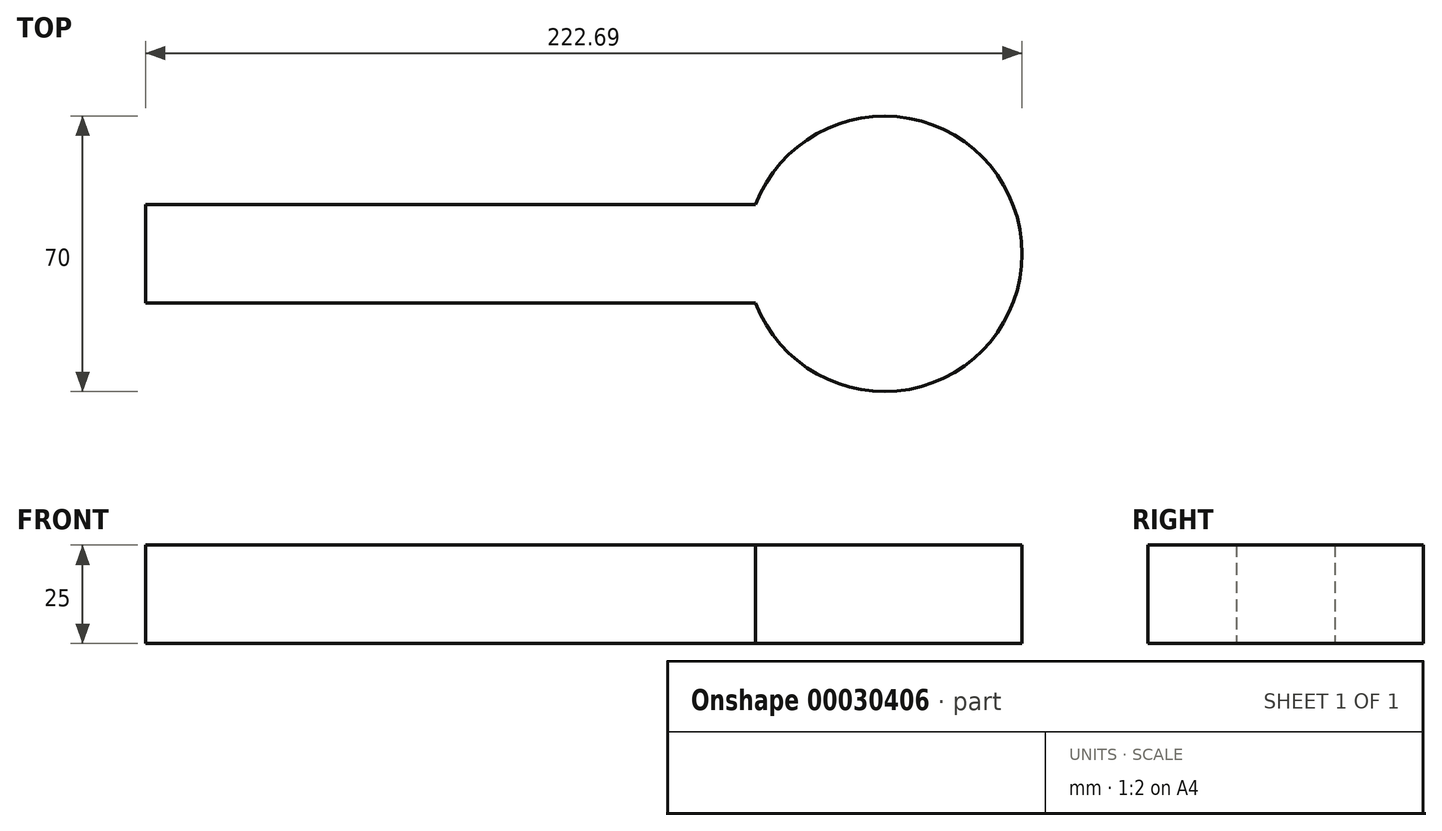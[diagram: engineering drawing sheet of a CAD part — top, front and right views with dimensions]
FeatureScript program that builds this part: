
annotation { "Feature Type Name" : "Feature", "Feature Type Description" : "" }
export const myFeature = defineFeature(function(context is Context, id is Id, definition is map)
    precondition{}
    {
        {
            var Q0;
            Q0=qCreatedBy(makeId("Top.planeOp"),FACE);
            var sketch = newSketch(context, id + "F0", { "sketchPlane" : qUnion([Q0])});
            skLineSegment(sketch, "E0.bottom", {"start": v(-86.93, 32.25) * mm, "end": v(68.07, 32.25) * mm});
            skLineSegment(sketch, "E0.top", {"start": v(-86.93, 7.25) * mm, "end": v(68.07, 7.25) * mm});
            skLineSegment(sketch, "E0.left", {"start": v(-86.93, 32.25) * mm, "end": v(-86.93, 7.25) * mm});
            skLineSegment(sketch, "E0.right", {"start": v(68.07, 32.25) * mm, "end": v(68.07, 7.25) * mm});
            skLineSegment(sketch, "E1.bottom", {"start": v(-86.93, 7.25) * mm, "end": v(-76.93, 7.25) * mm});
            skLineSegment(sketch, "E1.top", {"start": v(-86.93, -22.75) * mm, "end": v(-76.93, -22.75) * mm});
            skLineSegment(sketch, "E1.left", {"start": v(-86.93, 7.25) * mm, "end": v(-86.93, -22.75) * mm});
            skLineSegment(sketch, "E1.right", {"start": v(-76.93, 7.25) * mm, "end": v(-76.93, -22.75) * mm});
            skLineSegment(sketch, "E2.bottom", {"start": v(-69.04, 7.25) * mm, "end": v(-61.04, 7.25) * mm});
            skLineSegment(sketch, "E2.top", {"start": v(-69.04, -7.75) * mm, "end": v(-61.04, -7.75) * mm});
            skLineSegment(sketch, "E2.left", {"start": v(-69.04, 7.25) * mm, "end": v(-69.04, -7.75) * mm});
            skLineSegment(sketch, "E2.right", {"start": v(-61.04, 7.25) * mm, "end": v(-61.04, -7.75) * mm});
            skLineSegment(sketch, "E3", {"start": v(-52.63, 7.25) * mm, "end": v(-38.63, 7.25) * mm});
            skLineSegment(sketch, "E4", {"start": v(-38.63, 7.25) * mm, "end": v(-45.63, -7.75) * mm});
            skLineSegment(sketch, "E5", {"start": v(-45.63, -7.75) * mm, "end": v(-52.63, 7.25) * mm});
            skLineSegment(sketch, "E6", {"start": v(-45.63, 7.25) * mm, "end": v(-38.63, 7.25) * mm});
            skArc(sketch, "E7", {"start": v(68.07, 7.25) * mm, "mid": v(135.76, 19.75) * mm, "end": v(68.07, 32.25) * mm});
            skCircle(sketch, "E8", {"center": v(100.76, 19.75) * mm, "radius": 17.5 * mm});
            skLineSegment(sketch, "E9", {"start": v(-86.93, 19.75) * mm, "end": v(100.76, 19.75) * mm, "construction": true});
            skSolve(sketch);
        }
        {
            var Q0;
            Q0=makeQuery(id+"F0.imprint","IMPRINT",FACE,{"disambiguationData":[TD([[makeQuery(id+"F0.imprint","IMPRINT",EDGE,{"derivedFrom":sQuery(id+"F0.wireOp",EDGE,"E1.bottom")}),-1.0]])]});
            var Q1;
            Q1=makeQuery(id+"F0.imprint","IMPRINT",FACE,{"disambiguationData":[TD([[makeQuery(id+"F0.imprint","IMPRINT",EDGE,{"derivedFrom":sQuery(id+"F0.wireOp",EDGE,"E0.bottom")}),-1.0]])]});
            var Q2;
            Q2=makeQuery(id+"F0.imprint","IMPRINT",FACE,{"disambiguationData":[TD([[makeQuery(id+"F0.imprint","IMPRINT",EDGE,{"derivedFrom":sQuery(id+"F0.wireOp",EDGE,"E3")}),-1.0]])]});
            var Q3;
            Q3=makeQuery(id+"F0.imprint","IMPRINT",FACE,{"disambiguationData":[TD([[makeQuery(id+"F0.imprint","IMPRINT",EDGE,{"derivedFrom":sQuery(id+"F0.wireOp",EDGE,"E2.bottom")}),-1.0]])]});
            var Q4;
            Q4=makeQuery(id+"F0.imprint","IMPRINT",FACE,{"disambiguationData":[TD([[makeQuery(id+"F0.imprint","IMPRINT",EDGE,{"derivedFrom":sQuery(id+"F0.wireOp",EDGE,"E8")}),1.0]])]});
            var Q5;
            Q5=makeQuery(id+"F0.imprint","IMPRINT",FACE,{"disambiguationData":[TD([[makeQuery(id+"F0.imprint","IMPRINT",EDGE,{"derivedFrom":sQuery(id+"F0.wireOp",EDGE,"E0.right")}),1.0]])]});
            extrude(context, id + "F1", {"entities" : qUnion([Q0, Q1, Q2, Q3, Q4, Q5]), "depth" : 25 * mm});
        }
    });
